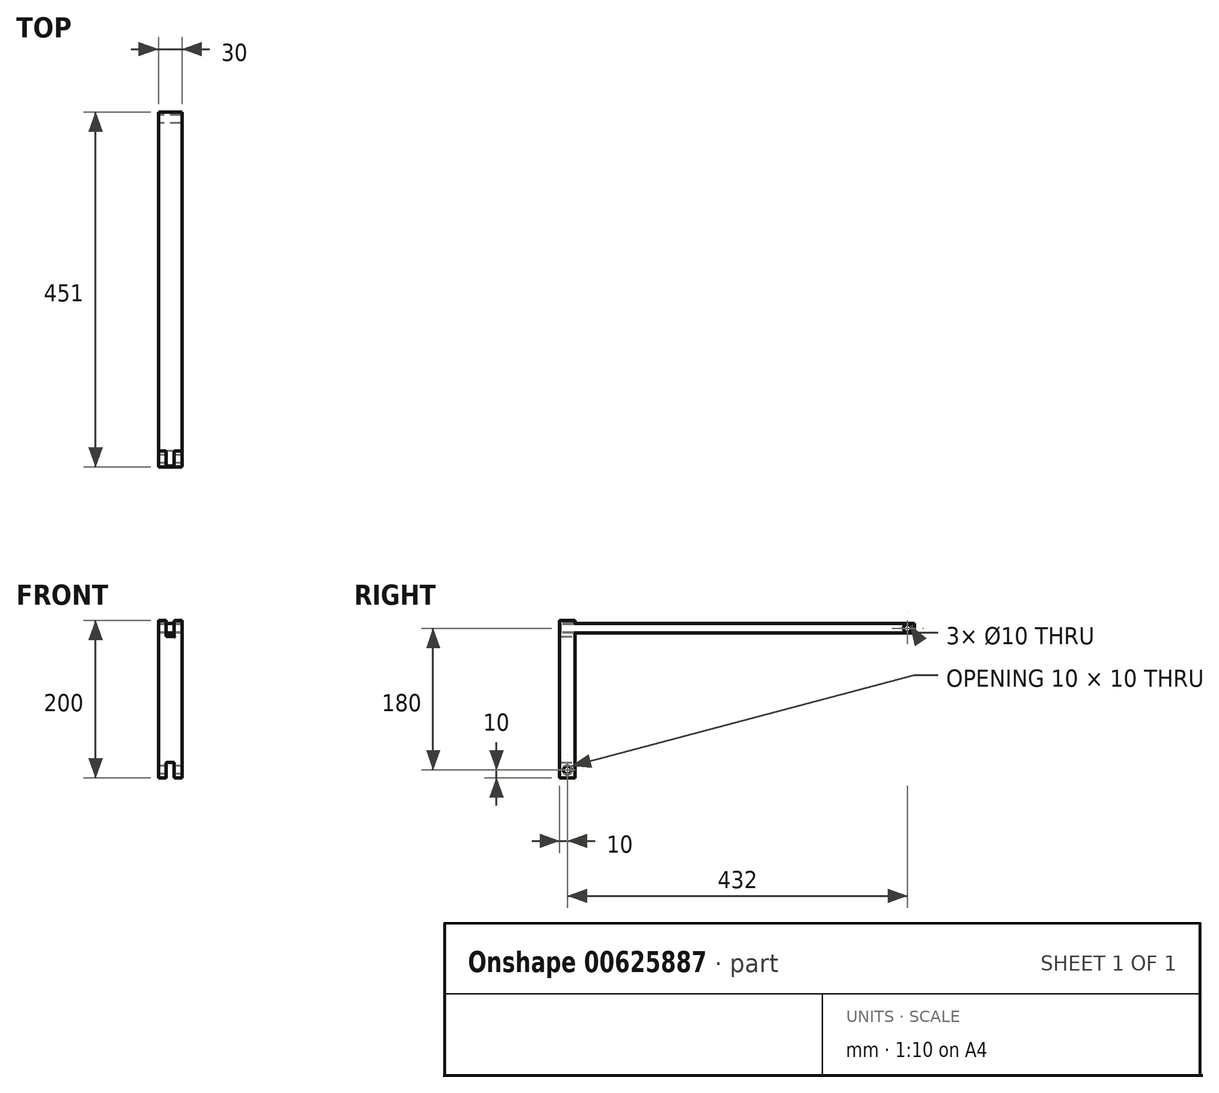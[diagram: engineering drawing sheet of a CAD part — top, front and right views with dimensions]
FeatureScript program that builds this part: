
annotation { "Feature Type Name" : "Feature", "Feature Type Description" : "" }
export const myFeature = defineFeature(function(context is Context, id is Id, definition is map)
    precondition{}
    {
        {
            var Q0;
            Q0=qCreatedBy(makeId("Front.planeOp"),FACE);
            var sketch = newSketch(context, id + "F0", { "sketchPlane" : qUnion([Q0])});
            skLineSegment(sketch, "E0", {"start": v(0, 100) * mm, "end": v(0, 0) * mm});
            skLineSegment(sketch, "E1", {"start": v(10, 100) * mm, "end": v(0, 100) * mm});
            skLineSegment(sketch, "E2", {"start": v(10, 80) * mm, "end": v(10, 100) * mm});
            skLineSegment(sketch, "E3", {"start": v(20, 80) * mm, "end": v(10, 80) * mm});
            skLineSegment(sketch, "E4", {"start": v(20, 80) * mm, "end": v(20, 100) * mm});
            skLineSegment(sketch, "E5", {"start": v(20, 100) * mm, "end": v(20, 100) * mm});
            skLineSegment(sketch, "E6", {"start": v(30, 100) * mm, "end": v(20, 100) * mm});
            skLineSegment(sketch, "E7", {"start": v(30, 100) * mm, "end": v(30, 0) * mm});
            skLineSegment(sketch, "E8", {"start": v(-6.07, 0) * mm, "end": v(31.83, 0) * mm, "construction": true});
            skLineSegment(sketch, "E9.MirrorCS", {"start": v(30, -100) * mm, "end": v(30, 0) * mm});
            skLineSegment(sketch, "E10.MirrorCS", {"start": v(0, -100) * mm, "end": v(0, 0) * mm});
            skLineSegment(sketch, "E11.MirrorCS", {"start": v(20, -80) * mm, "end": v(10, -80) * mm});
            skLineSegment(sketch, "E12.MirrorCS", {"start": v(10, -80) * mm, "end": v(10, -100) * mm});
            skLineSegment(sketch, "E13.MirrorCS", {"start": v(20, -80) * mm, "end": v(20, -100) * mm});
            skLineSegment(sketch, "E14.MirrorCS", {"start": v(10, -100) * mm, "end": v(0, -100) * mm});
            skLineSegment(sketch, "E15.MirrorCS", {"start": v(30, -100) * mm, "end": v(20, -100) * mm});
            skSolve(sketch);
        }
        {
            var Q0;
            Q0=makeQuery(id+"F0.imprint","IMPRINT",FACE,{"disambiguationData":[TD([[makeQuery(id+"F0.imprint","IMPRINT",EDGE,{"derivedFrom":sQuery(id+"F0.wireOp",EDGE,"E0")}),1.0]])]});
            extrude(context, id + "F1", {"entities" : qUnion([Q0]), "depth" : 20 * mm});
        }
        {
            var Q0;
            Q0=qCreatedBy(makeId("Right.planeOp"),FACE);
            var sketch = newSketch(context, id + "F2", { "sketchPlane" : qUnion([Q0])});
            skLineSegment(sketch, "E16", {"start": v(0, 80) * mm, "end": v(-20, 80) * mm, "construction": true});
            skLineSegment(sketch, "E17", {"start": v(-10, 80) * mm, "end": v(-10, 100) * mm, "construction": true});
            skCircle(sketch, "E18", {"center": v(-10, 90) * mm, "radius": 5 * mm});
            skCircle(sketch, "E19.MirrorC", {"center": v(-10, -90) * mm, "radius": 5 * mm});
            skSolve(sketch);
        }
        {
            var Q0;
            Q0=sQuery(id+"F2.wireOp",VERTEX,"E18.center");
            var Q1;
            Q1=sQuery(id+"F2.wireOp",VERTEX,"E19.MirrorC.center");
            var Q2;
            Q2=makeQuery(id+"F1.opExtrude","SWEPT_BODY",BODY,{"disambiguationData":[OSD([sQuery(id+"F0.wireOp",EDGE,"E0"),sQuery(id+"F0.wireOp",EDGE,"E1"),sQuery(id+"F0.wireOp",EDGE,"E2"),sQuery(id+"F0.wireOp",EDGE,"E3"),sQuery(id+"F0.wireOp",EDGE,"E4"),sQuery(id+"F0.wireOp",EDGE,"E6"),sQuery(id+"F0.wireOp",EDGE,"E7"),sQuery(id+"F0.wireOp",EDGE,"E9.MirrorCS"),sQuery(id+"F0.wireOp",EDGE,"E10.MirrorCS"),sQuery(id+"F0.wireOp",EDGE,"E11.MirrorCS"),sQuery(id+"F0.wireOp",EDGE,"E12.MirrorCS"),sQuery(id+"F0.wireOp",EDGE,"E13.MirrorCS"),sQuery(id+"F0.wireOp",EDGE,"E14.MirrorCS"),sQuery(id+"F0.wireOp",EDGE,"E15.MirrorCS")])]});
            hole(context, id + "F3", {"style" : HoleStyle.SIMPLE, "endStyle" : HoleEndStyle.THROUGH, "oppositeDirection" : true, "holeDiameter" : 10 * mm, "tappedDepth" : 12 * mm, "tapClearance" : 3, "locations" : qUnion([Q0, Q1]), "scope" : qUnion([Q2])});
        }
        {
            var Q0;
            Q0=makeQuery(id+"F1.opExtrude","CAP_FACE",FACE,{"disambiguationData":[OSD([sQuery(id+"F0.wireOp",EDGE,"E0"),sQuery(id+"F0.wireOp",EDGE,"E1"),sQuery(id+"F0.wireOp",EDGE,"E2"),sQuery(id+"F0.wireOp",EDGE,"E3"),sQuery(id+"F0.wireOp",EDGE,"E4"),sQuery(id+"F0.wireOp",EDGE,"E6"),sQuery(id+"F0.wireOp",EDGE,"E7"),sQuery(id+"F0.wireOp",EDGE,"E9.MirrorCS"),sQuery(id+"F0.wireOp",EDGE,"E10.MirrorCS"),sQuery(id+"F0.wireOp",EDGE,"E11.MirrorCS"),sQuery(id+"F0.wireOp",EDGE,"E12.MirrorCS"),sQuery(id+"F0.wireOp",EDGE,"E13.MirrorCS"),sQuery(id+"F0.wireOp",EDGE,"E14.MirrorCS"),sQuery(id+"F0.wireOp",EDGE,"E15.MirrorCS")])],"isStart":true});
            var Q1;
            Q1=makeQuery(id+"F1.opExtrude","CAP_EDGE",EDGE,{"disambiguationData":[OSD([sQuery(id+"F0.wireOp",EDGE,"E7"),sQuery(id+"F0.wireOp",EDGE,"E9.MirrorCS")])],"isStart":false});
            var Q2;
            Q2=makeQuery(id+"F1.opExtrude","CAP_FACE",FACE,{"disambiguationData":[OSD([sQuery(id+"F0.wireOp",EDGE,"E0"),sQuery(id+"F0.wireOp",EDGE,"E1"),sQuery(id+"F0.wireOp",EDGE,"E2"),sQuery(id+"F0.wireOp",EDGE,"E3"),sQuery(id+"F0.wireOp",EDGE,"E4"),sQuery(id+"F0.wireOp",EDGE,"E6"),sQuery(id+"F0.wireOp",EDGE,"E7"),sQuery(id+"F0.wireOp",EDGE,"E9.MirrorCS"),sQuery(id+"F0.wireOp",EDGE,"E10.MirrorCS"),sQuery(id+"F0.wireOp",EDGE,"E11.MirrorCS"),sQuery(id+"F0.wireOp",EDGE,"E12.MirrorCS"),sQuery(id+"F0.wireOp",EDGE,"E13.MirrorCS"),sQuery(id+"F0.wireOp",EDGE,"E14.MirrorCS"),sQuery(id+"F0.wireOp",EDGE,"E15.MirrorCS")])],"isStart":false});
            var Q3;
            Q3=makeQuery(id+"F1.opExtrude","SWEPT_FACE",FACE,{"disambiguationData":[OSD([sQuery(id+"F0.wireOp",EDGE,"E6")])]});
            var Q4;
            Q4=makeQuery(id+"F1.opExtrude","SWEPT_FACE",FACE,{"disambiguationData":[OSD([sQuery(id+"F0.wireOp",EDGE,"E1")])]});
            var Q5;
            Q5=makeQuery(id+"F1.opExtrude","SWEPT_FACE",FACE,{"disambiguationData":[OSD([sQuery(id+"F0.wireOp",EDGE,"E15.MirrorCS")])]});
            var Q6;
            Q6=makeQuery(id+"F1.opExtrude","SWEPT_FACE",FACE,{"disambiguationData":[OSD([sQuery(id+"F0.wireOp",EDGE,"E14.MirrorCS")])]});
            var Q7;
            Q7=makeQuery(id+"F1.opExtrude","SWEPT_FACE",FACE,{"disambiguationData":[OSD([sQuery(id+"F0.wireOp",EDGE,"E11.MirrorCS")])]});
            fillet(context, id + "F4", {"entities" : qUnion([Q0, Q1, Q2, Q3, Q4, Q5, Q6, Q7]), "radius" : 1 * mm, "tangentPropagation" : true, "allowEdgeOverflow" : false});
        }
        {
            var Q0;
            Q0=makeQuery(id+"F1.opExtrude","SWEPT_FACE",FACE,{"disambiguationData":[OSD([sQuery(id+"F0.wireOp",EDGE,"E2")])]});
            var sketch = newSketch(context, id + "F5", { "sketchPlane" : qUnion([Q0])});
            skLineSegment(sketch, "E20.bottom", {"start": v(-19, 84) * mm, "end": v(431, 84) * mm});
            skLineSegment(sketch, "E20.top", {"start": v(-19, 96) * mm, "end": v(431, 96) * mm});
            skLineSegment(sketch, "E20.left", {"start": v(-19, 84) * mm, "end": v(-19, 96) * mm});
            skLineSegment(sketch, "E20.right", {"start": v(431, 84) * mm, "end": v(431, 96) * mm});
            skLineSegment(sketch, "E21", {"start": v(-10, 90) * mm, "end": v(-38.52, 90) * mm, "construction": true});
            skCircle(sketch, "E22", {"center": v(-10, 90) * mm, "radius": 5 * mm});
            skLineSegment(sketch, "E23", {"start": v(206, 96) * mm, "end": v(206, 84) * mm, "construction": true});
            skCircle(sketch, "E24.MirrorC", {"center": v(422, 90) * mm, "radius": 5 * mm});
            skSolve(sketch);
        }
        {
            var Q0;
            Q0=qSketchRegion(id+"F5",true);
            var Q1;
            Q1=makeQuery(id+"F1.opExtrude","SWEPT_FACE",FACE,{"disambiguationData":[OSD([sQuery(id+"F0.wireOp",EDGE,"E4")])]});
            extrude(context, id + "F6", {"entities" : qUnion([Q0]), "endBound" : BoundingType.UP_TO_SURFACE, "endBoundEntityFace" : qUnion([Q1]), "depth" : 25 * mm});
        }
        {
            var Q0;
            Q0=makeQuery(id+"F6.opExtrude","SWEPT_FACE",FACE,{"disambiguationData":[OSD([sQuery(id+"F5.wireOp",EDGE,"E20.top")])]});
            var Q1;
            Q1=makeQuery(id+"F6.opExtrude","SWEPT_FACE",FACE,{"disambiguationData":[OSD([sQuery(id+"F5.wireOp",EDGE,"E20.right")])]});
            var Q2;
            Q2=makeQuery(id+"F6.opExtrude","SWEPT_FACE",FACE,{"disambiguationData":[OSD([sQuery(id+"F5.wireOp",EDGE,"E20.bottom")])]});
            var Q3;
            Q3=makeQuery(id+"F6.opExtrude","SWEPT_FACE",FACE,{"disambiguationData":[OSD([sQuery(id+"F5.wireOp",EDGE,"E20.left")])]});
            fillet(context, id + "F7", {"entities" : qUnion([Q0, Q1, Q2, Q3]), "radius" : 1 * mm, "tangentPropagation" : true, "allowEdgeOverflow" : false});
        }
        {
            var Q0;
            Q0=makeQuery(id+"F5.imprint","IMPRINT",FACE,{"disambiguationData":[TD([[makeQuery(id+"F5.imprint","IMPRINT",EDGE,{"derivedFrom":sQuery(id+"F5.wireOp",EDGE,"E22")}),1.0]])]});
            var Q1;
            Q1=makeQuery(id+"F5.imprint","IMPRINT",FACE,{"disambiguationData":[TD([[makeQuery(id+"F5.imprint","IMPRINT",EDGE,{"derivedFrom":sQuery(id+"F5.wireOp",EDGE,"E24.MirrorC")}),-1.0]])]});
            extrude(context, id + "F8", {"entities" : qUnion([Q0, Q1]), "operationType" : NewBodyOperationType.ADD, "depth" : 20 * mm, "hasSecondDirection" : true, "secondDirectionOppositeDirection" : true, "secondDirectionDepth" : 10 * mm});
        }
    });
